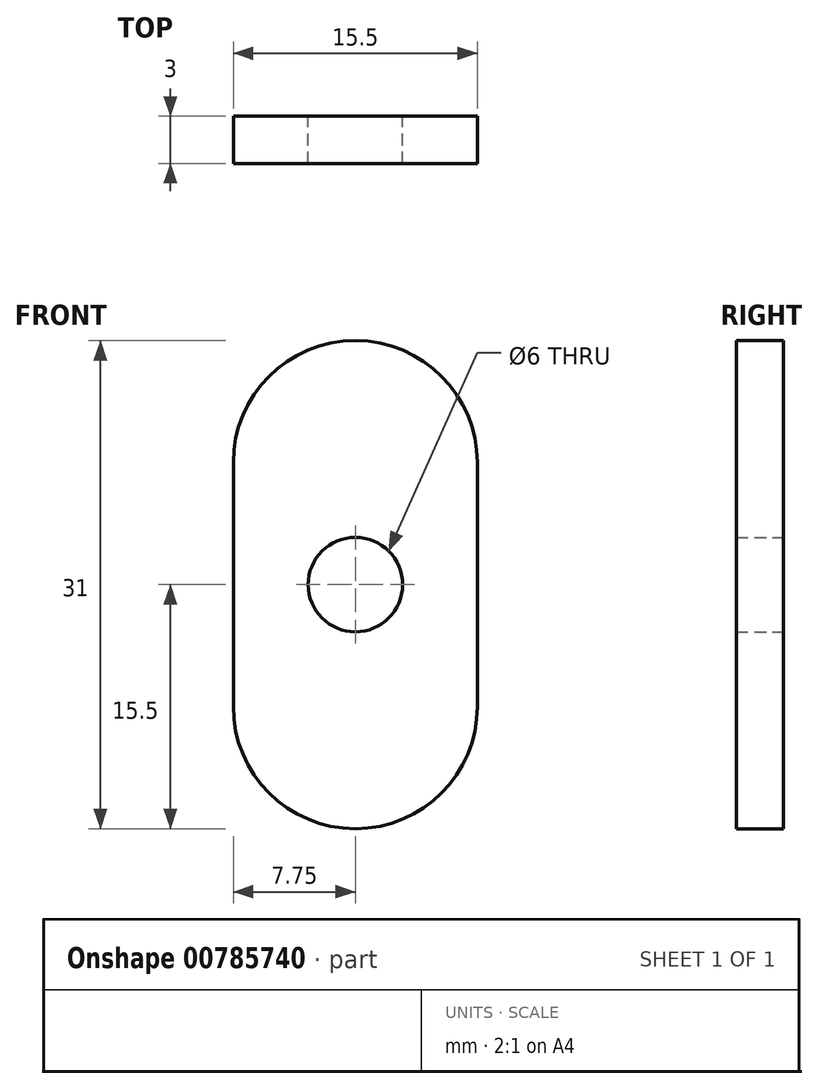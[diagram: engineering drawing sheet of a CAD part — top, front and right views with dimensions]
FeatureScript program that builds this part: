
annotation { "Feature Type Name" : "Feature", "Feature Type Description" : "" }
export const myFeature = defineFeature(function(context is Context, id is Id, definition is map)
    precondition{}
    {
        {
            var Q0;
            Q0=qCreatedBy(makeId("Front.planeOp"),FACE);
            var sketch = newSketch(context, id + "F0", { "sketchPlane" : qUnion([Q0])});
            skLineSegment(sketch, "E0.left", {"start": v(-7.75, 7.75) * mm, "end": v(-7.75, -7.75) * mm});
            skLineSegment(sketch, "E0.right", {"start": v(7.75, 7.75) * mm, "end": v(7.75, -7.75) * mm});
            skPoint(sketch, "E0.middle", {"position": v(0, 0) * mm});
            skArc(sketch, "E1", {"start": v(7.75, 7.75) * mm, "mid": v(0, 15.5) * mm, "end": v(-7.75, 7.75) * mm});
            skArc(sketch, "E2", {"start": v(-7.75, -7.75) * mm, "mid": v(0, -15.5) * mm, "end": v(7.75, -7.75) * mm});
            skCircle(sketch, "E3", {"center": v(0, 0) * mm, "radius": 3 * mm});
            skSolve(sketch);
        }
        {
            var Q0;
            Q0=qSketchRegion(id+"F0",true);
            extrude(context, id + "F1", {"entities" : qUnion([Q0]), "depth" : 3 * mm, "offsetDistance" : 25 * mm});
        }
    });
